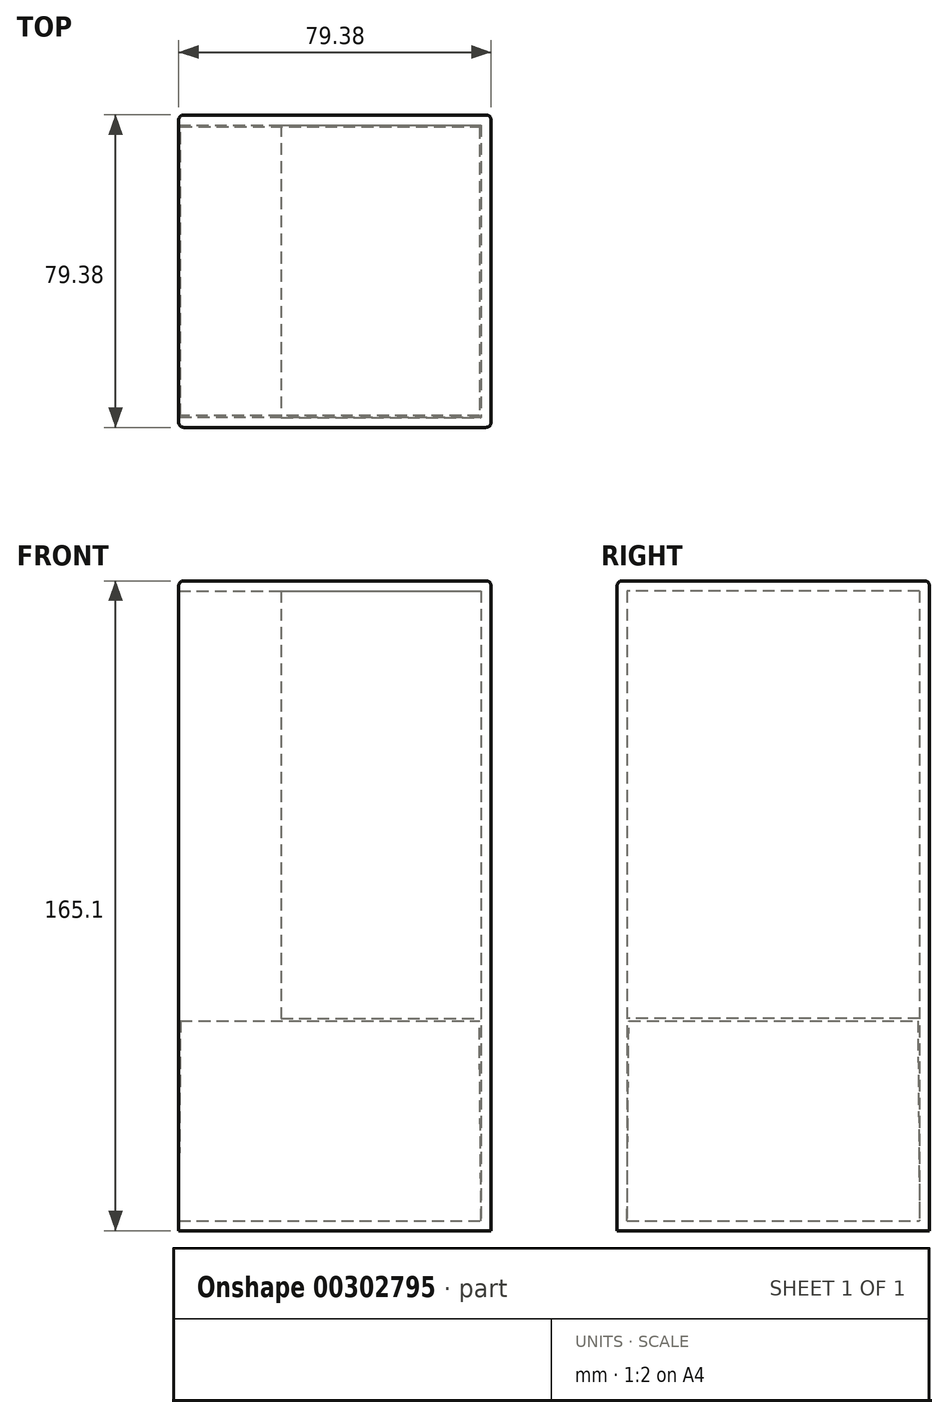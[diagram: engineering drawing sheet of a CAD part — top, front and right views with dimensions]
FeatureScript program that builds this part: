
annotation { "Feature Type Name" : "Feature", "Feature Type Description" : "" }
export const myFeature = defineFeature(function(context is Context, id is Id, definition is map)
    precondition{}
    {
        {
            var Q0;
            Q0=qCreatedBy(makeId("Top.planeOp"),FACE);
            var sketch = newSketch(context, id + "F0", { "sketchPlane" : qUnion([Q0])});
            skLineSegment(sketch, "E0.bottom", {"start": v(39.69, 39.69) * mm, "end": v(-39.69, 39.69) * mm});
            skLineSegment(sketch, "E0.top", {"start": v(39.69, -39.69) * mm, "end": v(-39.69, -39.69) * mm});
            skLineSegment(sketch, "E0.left", {"start": v(39.69, 39.69) * mm, "end": v(39.69, -39.69) * mm});
            skLineSegment(sketch, "E0.right", {"start": v(-39.69, 39.69) * mm, "end": v(-39.69, -39.69) * mm});
            skPoint(sketch, "E0.middle", {"position": v(0, 0) * mm});
            skSolve(sketch);
        }
        {
            var Q0;
            Q0=qSketchRegion(id+"F0",true);
            extrude(context, id + "F1", {"entities" : qUnion([Q0]), "depth" : 165.1 * mm});
        }
        {
            var Q0;
            Q0=makeQuery(id+"F1.opExtrude","SWEPT_EDGE",EDGE,{"disambiguationData":[OSD([sQuery(id+"F0.wireOp",EDGE,"E0.top"),sQuery(id+"F0.wireOp",EDGE,"E0.left")])]});
            var Q1;
            Q1=makeQuery(id+"F1.opExtrude","CAP_EDGE",EDGE,{"disambiguationData":[OSD([sQuery(id+"F0.wireOp",EDGE,"E0.left")])],"isStart":false});
            var Q2;
            Q2=makeQuery(id+"F1.opExtrude","SWEPT_EDGE",EDGE,{"disambiguationData":[OSD([sQuery(id+"F0.wireOp",EDGE,"E0.bottom"),sQuery(id+"F0.wireOp",EDGE,"E0.left")])]});
            var Q3;
            Q3=makeQuery(id+"F1.opExtrude","SWEPT_EDGE",EDGE,{"disambiguationData":[OSD([sQuery(id+"F0.wireOp",EDGE,"E0.top"),sQuery(id+"F0.wireOp",EDGE,"E0.right")])]});
            var Q4;
            Q4=makeQuery(id+"F1.opExtrude","CAP_EDGE",EDGE,{"disambiguationData":[OSD([sQuery(id+"F0.wireOp",EDGE,"E0.top")])],"isStart":false});
            var Q5;
            Q5=makeQuery(id+"F1.opExtrude","CAP_EDGE",EDGE,{"disambiguationData":[OSD([sQuery(id+"F0.wireOp",EDGE,"E0.bottom")])],"isStart":false});
            var Q6;
            Q6=makeQuery(id+"F1.opExtrude","SWEPT_EDGE",EDGE,{"disambiguationData":[OSD([sQuery(id+"F0.wireOp",EDGE,"E0.bottom"),sQuery(id+"F0.wireOp",EDGE,"E0.right")])]});
            var Q7;
            Q7=makeQuery(id+"F1.opExtrude","CAP_EDGE",EDGE,{"disambiguationData":[OSD([sQuery(id+"F0.wireOp",EDGE,"E0.right")])],"isStart":false});
            fillet(context, id + "F2", {"entities" : qUnion([Q0, Q1, Q2, Q3, Q4, Q5, Q6, Q7]), "radius" : 1.27 * mm, "tangentPropagation" : true, "allowEdgeOverflow" : false});
        }
        {
            var Q0;
            Q0=makeQuery(id+"F1.opExtrude","SWEPT_FACE",FACE,{"disambiguationData":[OSD([sQuery(id+"F0.wireOp",EDGE,"E0.right")])]});
            shell(context, id + "F3", {"entities" : qUnion([Q0]), "thickness" : 2.54 * mm});
        }
        {
            var Q0;
            {var subQ0=sQuery(id+"F0.wireOp",EDGE,"E0.right");var subQ1=sQuery(id+"F0.wireOp",EDGE,"E0.left");var subQ2=sQuery(id+"F0.wireOp",EDGE,"E0.top");var subQ3=sQuery(id+"F0.wireOp",EDGE,"E0.bottom");Q0=makeQuery(id+"F3.opShell","OFFSET_FACE",FACE,{"disambiguationData":[OSD([subQ3,subQ2,subQ1,subQ0]),TDD([makeQuery(id+"F1.opExtrude","CAP_FACE",FACE,{"disambiguationData":[OSD([subQ3,subQ2,subQ1,subQ0])],"isStart":true})])]});}
            var sketch = newSketch(context, id + "F4", { "sketchPlane" : qUnion([Q0])});
            skLineSegment(sketch, "E1.bottom", {"start": v(37.15, 37.15) * mm, "end": v(-39.69, 37.15) * mm});
            skLineSegment(sketch, "E1.top", {"start": v(37.15, -37.15) * mm, "end": v(-39.69, -37.15) * mm});
            skLineSegment(sketch, "E1.left", {"start": v(37.15, 37.15) * mm, "end": v(37.15, -37.15) * mm});
            skLineSegment(sketch, "E1.right", {"start": v(-39.69, 37.15) * mm, "end": v(-39.69, -37.15) * mm});
            skSolve(sketch);
        }
        {
            var Q0;
            Q0 = qSketchRegion(id + "F4", true);
            extrude(context, id + "F5", {"entities" : qUnion([Q0]), "depth" : 50.8 * mm, "offsetDistance" : 25.4 * mm, "hasDraft" : true, "draftAngle" : .5 * degree, "draftPullDirection" : true});
        }
        {
            var Q0;
            Q0=makeQuery(id+"F3.opShell","OFFSET_FACE",FACE,{"disambiguationData":[OSD([sQuery(id+"F0.wireOp",EDGE,"E0.left")])]});
            var sketch = newSketch(context, id + "F6", { "sketchPlane" : qUnion([Q0])});
            skLineSegment(sketch, "E2.bottom", {"start": v(-37.15, 53.95) * mm, "end": v(37.15, 53.95) * mm});
            skLineSegment(sketch, "E2.top", {"start": v(-37.15, 162.56) * mm, "end": v(37.15, 162.56) * mm});
            skLineSegment(sketch, "E2.left", {"start": v(-37.15, 53.95) * mm, "end": v(-37.15, 162.56) * mm});
            skLineSegment(sketch, "E2.right", {"start": v(37.15, 53.95) * mm, "end": v(37.15, 162.56) * mm});
            skSolve(sketch);
        }
        {
            var Q0;
            Q0 = qSketchRegion(id + "F6", true);
            extrude(context, id + "F7", {"entities" : qUnion([Q0]), "depth" : 50.8 * mm, "offsetDistance" : 25.4 * mm});
        }
    });
